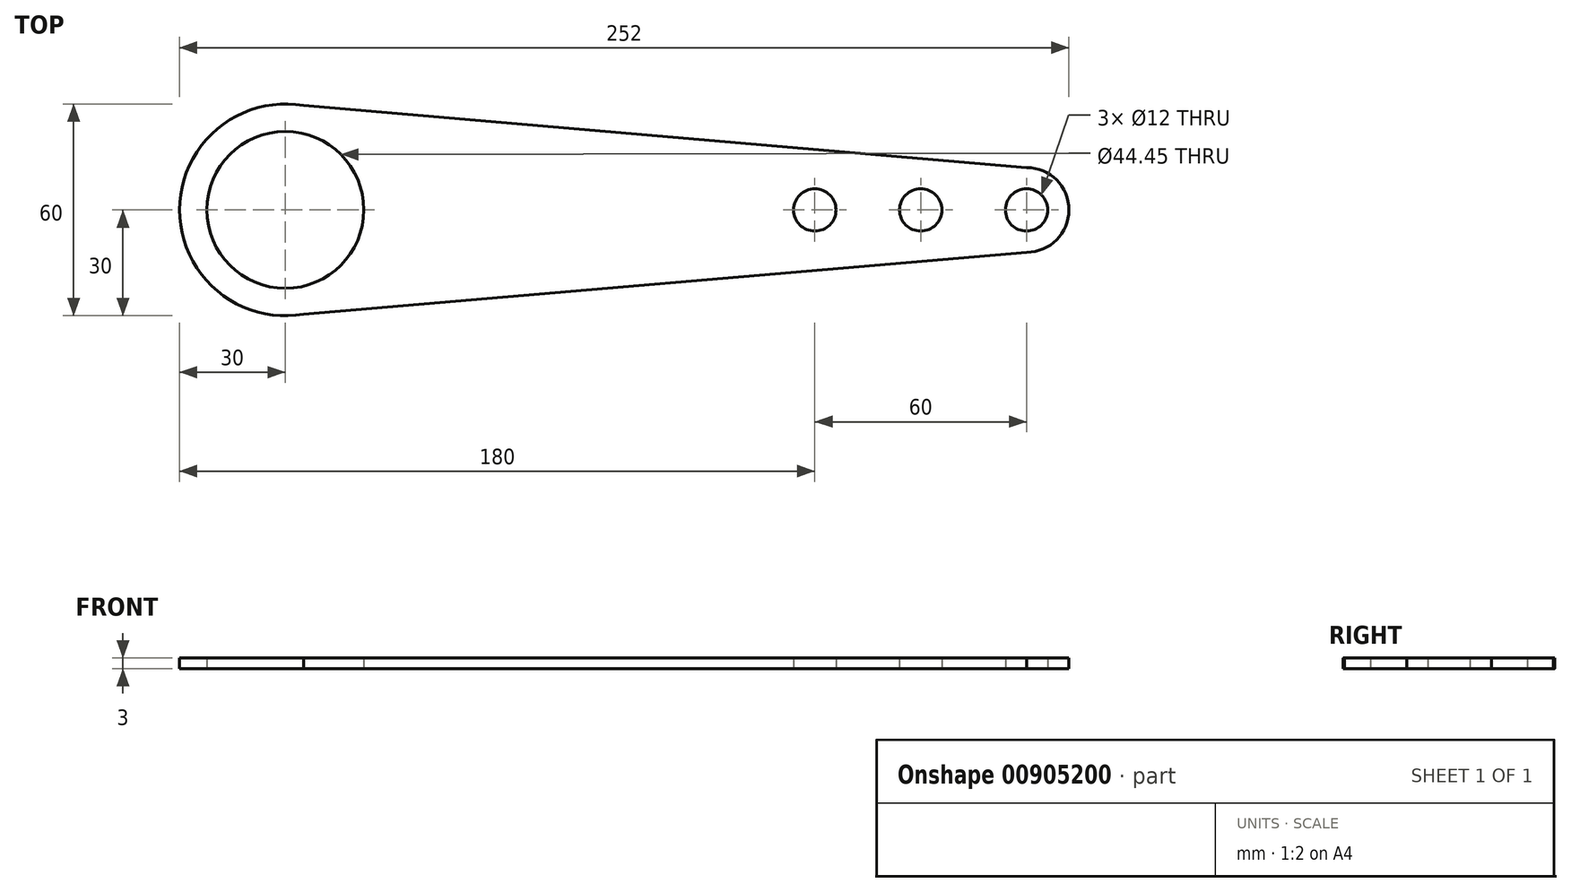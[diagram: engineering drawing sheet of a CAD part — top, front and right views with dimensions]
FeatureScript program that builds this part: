
annotation { "Feature Type Name" : "Feature", "Feature Type Description" : "" }
export const myFeature = defineFeature(function(context is Context, id is Id, definition is map)
    precondition{}
    {
        {
            var Q0;
            Q0=qCreatedBy(makeId("Top.planeOp"),FACE);
            var sketch = newSketch(context, id + "F0", { "sketchPlane" : qUnion([Q0])});
            skCircle(sketch, "E0", {"center": v(0, 0) * mm, "radius": 22.23 * mm});
            skCircle(sketch, "E1", {"center": v(180, 0) * mm, "radius": 6 * mm});
            skCircle(sketch, "E2", {"center": v(150, 0) * mm, "radius": 6 * mm});
            skCircle(sketch, "E3", {"center": v(210, 0) * mm, "radius": 6 * mm});
            skArc(sketch, "E4", {"start": v(5.1, 29.56) * mm, "mid": v(-30, 0) * mm, "end": v(5.1, -29.56) * mm});
            skArc(sketch, "E5", {"start": v(210, -12) * mm, "mid": v(222, 0) * mm, "end": v(210, 12) * mm});
            skLineSegment(sketch, "E6", {"start": v(5.1, -29.56) * mm, "end": v(210, -12) * mm});
            skLineSegment(sketch, "E7", {"start": v(5.1, 29.56) * mm, "end": v(210, 12) * mm});
            skPoint(sketch, "E8.orphan", {"position": v(0, -30) * mm});
            skPoint(sketch, "E9.orphan", {"position": v(0, 30) * mm});
            skSolve(sketch);
        }
        {
            var Q0;
            Q0 = qSketchRegion(id + "F0", true);
            extrude(context, id + "F1", {"entities" : qUnion([Q0]), "depth" : 3 * mm, "offsetDistance" : 25 * mm});
        }
    });
